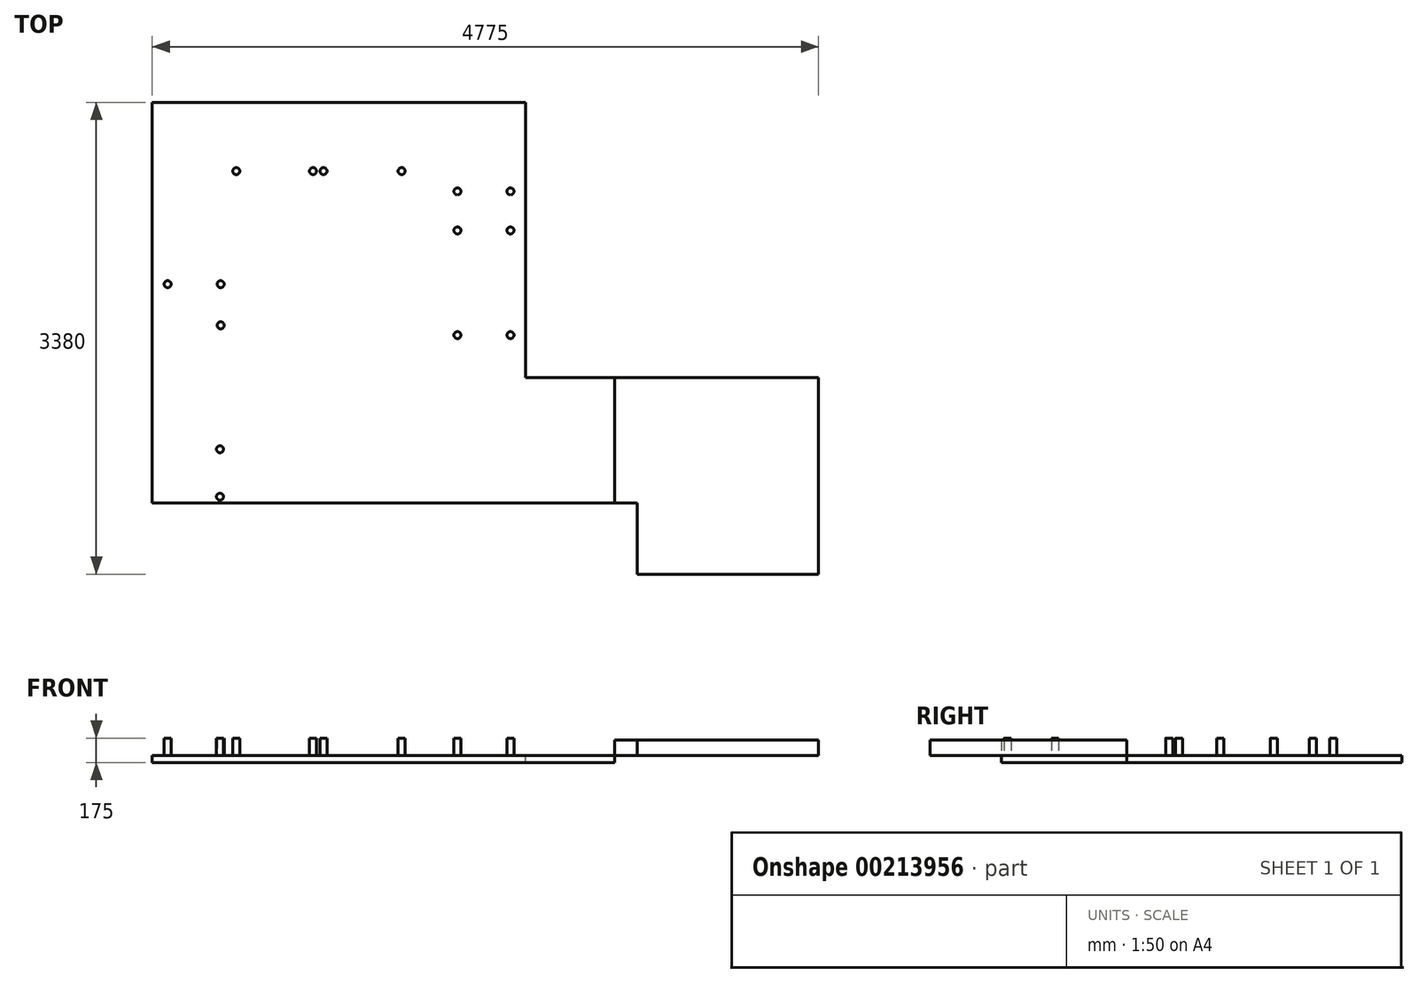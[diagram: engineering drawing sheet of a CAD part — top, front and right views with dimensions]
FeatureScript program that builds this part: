
annotation { "Feature Type Name" : "Feature", "Feature Type Description" : "" }
export const myFeature = defineFeature(function(context is Context, id is Id, definition is map)
    precondition{}
    {
        {
            var Q0;
            Q0=qCreatedBy(makeId("Top.planeOp"),FACE);
            var sketch = newSketch(context, id + "F0", { "sketchPlane" : qUnion([Q0])});
            skLineSegment(sketch, "E0", {"start": v(-610, -2257.95) * mm, "end": v(2065, -2257.95) * mm});
            skLineSegment(sketch, "E1", {"start": v(0, -2257.95) * mm, "end": v(0, -1827.95) * mm, "construction": true});
            skLineSegment(sketch, "E2", {"start": v(-500, 0.05) * mm, "end": v(1457, 0.05) * mm, "construction": true});
            skLineSegment(sketch, "E3", {"start": v(1457, 0.05) * mm, "end": v(1457, -1099.95) * mm, "construction": true});
            skLineSegment(sketch, "E4", {"start": v(1457, -1099.95) * mm, "end": v(2065, -1099.95) * mm, "construction": true});
            skLineSegment(sketch, "E5", {"start": v(2065, -1357.95) * mm, "end": v(2065, 612.05) * mm});
            skLineSegment(sketch, "E6", {"start": v(2065, 612.05) * mm, "end": v(-610, 612.05) * mm});
            skLineSegment(sketch, "E7", {"start": v(-610, 612.05) * mm, "end": v(-610, -2257.95) * mm});
            skLineSegment(sketch, "E8", {"start": v(0, -1029.95) * mm, "end": v(-536.33, -1029.95) * mm, "construction": true});
            skLineSegment(sketch, "E9", {"start": v(-610, -1013.95) * mm, "end": v(-536.33, -1013.95) * mm, "construction": true});
            skLineSegment(sketch, "E10", {"start": v(-536.33, -1843.95) * mm, "end": v(-610, -1843.95) * mm, "construction": true});
            skLineSegment(sketch, "E11", {"start": v(-536.33, -1013.95) * mm, "end": v(-536.33, -1029.95) * mm, "construction": true});
            skLineSegment(sketch, "E12.trimOffspring", {"start": v(0, -1029.95) * mm, "end": v(0, -644.95) * mm, "construction": true});
            skLineSegment(sketch, "E13.trimOffspring", {"start": v(-536.33, -1827.95) * mm, "end": v(-536.33, -1843.95) * mm, "construction": true});
            skLineSegment(sketch, "E14.trimOffspring", {"start": v(-536.33, -1827.95) * mm, "end": v(0, -1827.95) * mm, "construction": true});
            skCircle(sketch, "E15", {"center": v(1577, -1054.95) * mm, "radius": 25 * mm, "construction": true});
            skCircle(sketch, "E16", {"center": v(1957, -1054.95) * mm, "radius": 25 * mm, "construction": true});
            skCircle(sketch, "E17", {"center": v(1577, -304.95) * mm, "radius": 25 * mm, "construction": true});
            skCircle(sketch, "E18", {"center": v(1957, -304.95) * mm, "radius": 25 * mm, "construction": true});
            skCircle(sketch, "E19", {"center": v(1577, -24.95) * mm, "radius": 25 * mm, "construction": true});
            skCircle(sketch, "E20", {"center": v(1957, -24.95) * mm, "radius": 25 * mm, "construction": true});
            skCircle(sketch, "E21", {"center": v(617, 120.05) * mm, "radius": 25 * mm, "construction": true});
            skCircle(sketch, "E22", {"center": v(1177, 120.05) * mm, "radius": 25 * mm, "construction": true});
            skCircle(sketch, "E23", {"center": v(542, 120.05) * mm, "radius": 25 * mm, "construction": true});
            skCircle(sketch, "E24", {"center": v(-8, 120.05) * mm, "radius": 25 * mm, "construction": true});
            skLineSegment(sketch, "E25", {"start": v(0, -644.95) * mm, "end": v(-500, -644.95) * mm, "construction": true});
            skCircle(sketch, "E26", {"center": v(-120, -689.95) * mm, "radius": 25 * mm, "construction": true});
            skCircle(sketch, "E27", {"center": v(-120, -984.95) * mm, "radius": 25 * mm, "construction": true});
            skCircle(sketch, "E28", {"center": v(-125, -1872.95) * mm, "radius": 25 * mm, "construction": true});
            skCircle(sketch, "E29", {"center": v(-125, -2212.95) * mm, "radius": 25 * mm, "construction": true});
            skCircle(sketch, "E30", {"center": v(-500, -689.95) * mm, "radius": 25 * mm, "construction": true});
            skLineSegment(sketch, "E31", {"start": v(2065, -2257.95) * mm, "end": v(2705, -2257.95) * mm});
            skLineSegment(sketch, "E32", {"start": v(2705, -2257.95) * mm, "end": v(2705, -1357.95) * mm});
            skLineSegment(sketch, "E33", {"start": v(2705, -1357.95) * mm, "end": v(2065, -1357.95) * mm});
            skSolve(sketch);
        }
        {
            var Q0;
            Q0 = qSketchRegion(id + "F0", true);
            extrude(context, id + "F1", {"entities" : qUnion([Q0]), "oppositeDirection" : true, "depth" : 50 * mm});
        }
        {
            var Q0;
            Q0=makeQuery(id+"F0.imprint","IMPRINT",FACE,{"disambiguationData":[TD([[makeQuery(id+"F0.imprint","IMPRINT",EDGE,{"derivedFrom":sQuery(id+"F0.wireOp",EDGE,"E0")}),1.0]])]});
            var sketch = newSketch(context, id + "F2", { "sketchPlane" : qUnion([Q0])});
            skLineSegment(sketch, "E34.0", {"start": v(2705, -2257.95) * mm, "end": v(2705, -1357.95) * mm});
            skLineSegment(sketch, "E35", {"start": v(2705, -1357.95) * mm, "end": v(4165, -1357.95) * mm});
            skLineSegment(sketch, "E36", {"start": v(4165, -1357.95) * mm, "end": v(4165, -2767.95) * mm});
            skLineSegment(sketch, "E37", {"start": v(4165, -2767.95) * mm, "end": v(2865, -2767.95) * mm});
            skLineSegment(sketch, "E38", {"start": v(2865, -2767.95) * mm, "end": v(2865, -2257.95) * mm});
            skLineSegment(sketch, "E39", {"start": v(2705, -2257.95) * mm, "end": v(2865, -2257.95) * mm});
            skSolve(sketch);
        }
        {
            var Q0;
            Q0 = qSketchRegion(id + "F2", true);
            extrude(context, id + "F3", {"entities" : qUnion([Q0]), "depth" : 110 * mm});
        }
        {
            var Q0;
            Q0=makeQuery(id+"F1.opExtrude","CAP_FACE",FACE,{"disambiguationData":[OSD([sQuery(id+"F0.wireOp",EDGE,"E0"),sQuery(id+"F0.wireOp",EDGE,"E5"),sQuery(id+"F0.wireOp",EDGE,"E6"),sQuery(id+"F0.wireOp",EDGE,"E7")])],"isStart":true});
            var sketch = newSketch(context, id + "F4", { "sketchPlane" : qUnion([Q0])});
            skCircle(sketch, "E40.0", {"center": v(-8, 120.05) * mm, "radius": 25 * mm});
            skCircle(sketch, "E40.1", {"center": v(-120, -689.95) * mm, "radius": 25 * mm});
            skCircle(sketch, "E40.2", {"center": v(-500, -689.95) * mm, "radius": 25 * mm});
            skCircle(sketch, "E40.3", {"center": v(-120, -984.95) * mm, "radius": 25 * mm});
            skCircle(sketch, "E40.4", {"center": v(617, 120.05) * mm, "radius": 25 * mm});
            skCircle(sketch, "E40.5", {"center": v(542, 120.05) * mm, "radius": 25 * mm});
            skCircle(sketch, "E40.6", {"center": v(1177, 120.05) * mm, "radius": 25 * mm});
            skCircle(sketch, "E40.7", {"center": v(1577, -24.95) * mm, "radius": 25 * mm});
            skCircle(sketch, "E40.8", {"center": v(1577, -304.95) * mm, "radius": 25 * mm});
            skCircle(sketch, "E40.9", {"center": v(-125, -1872.95) * mm, "radius": 25 * mm});
            skCircle(sketch, "E40.10", {"center": v(-125, -2212.95) * mm, "radius": 25 * mm});
            skCircle(sketch, "E40.11", {"center": v(1957, -304.95) * mm, "radius": 25 * mm});
            skCircle(sketch, "E40.12", {"center": v(1957, -24.95) * mm, "radius": 25 * mm});
            skCircle(sketch, "E40.13", {"center": v(1957, -1054.95) * mm, "radius": 25 * mm});
            skCircle(sketch, "E40.14", {"center": v(1577, -1054.95) * mm, "radius": 25 * mm});
            skSolve(sketch);
        }
        {
            var Q0;
            Q0 = qSketchRegion(id + "F4", true);
            extrude(context, id + "F5", {"entities" : qUnion([Q0]), "operationType" : NewBodyOperationType.ADD, "depth" : 125 * mm});
        }
    });
